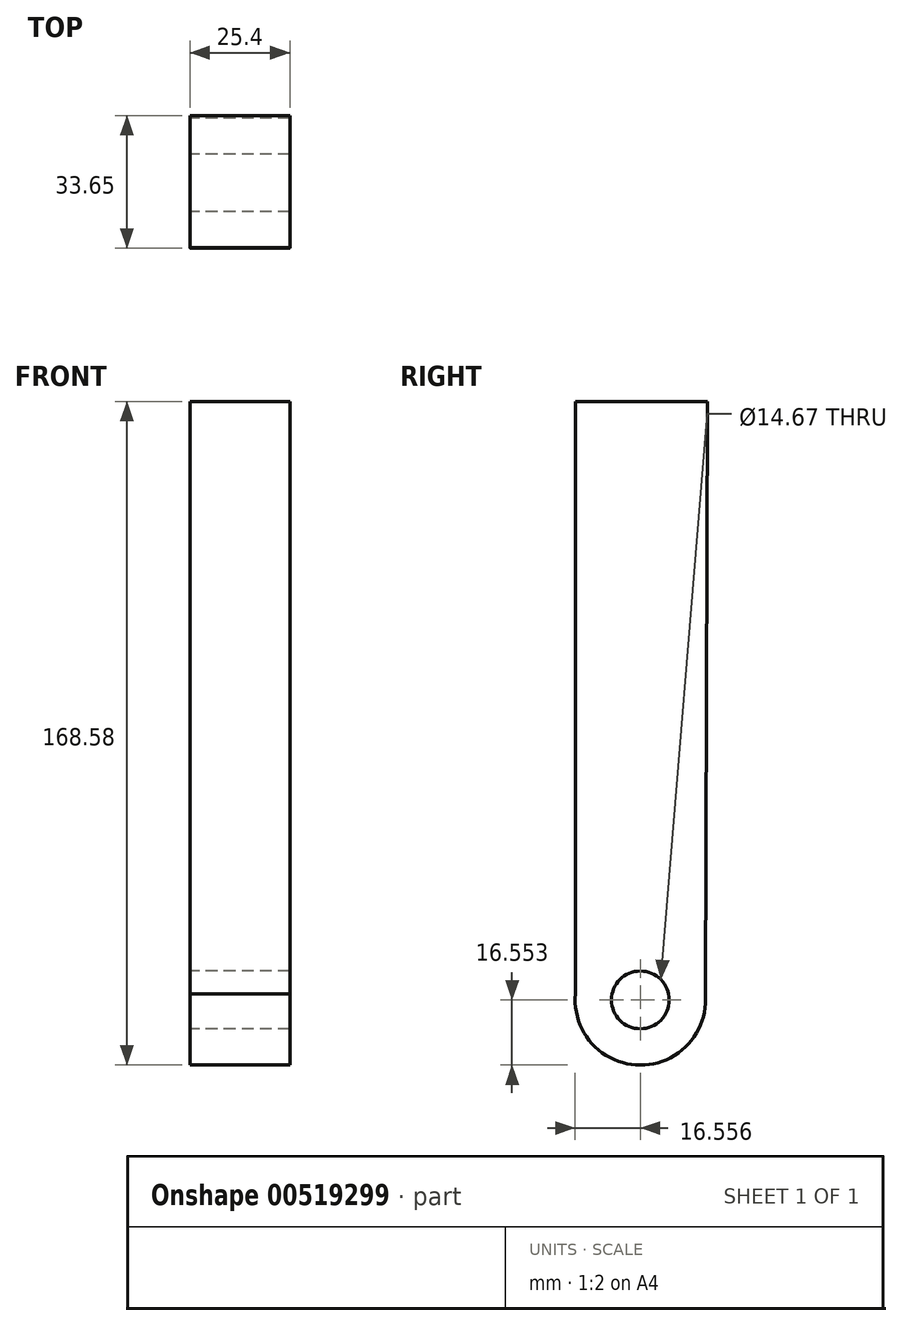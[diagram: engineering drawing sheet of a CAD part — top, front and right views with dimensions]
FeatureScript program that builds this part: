
annotation { "Feature Type Name" : "Feature", "Feature Type Description" : "" }
export const myFeature = defineFeature(function(context is Context, id is Id, definition is map)
    precondition{}
    {
        {
            var Q0;
            Q0=qCreatedBy(makeId("Right.planeOp"),FACE);
            var sketch = newSketch(context, id + "F0", { "sketchPlane" : qUnion([Q0])});
            skLineSegment(sketch, "E0", {"start": v(0, -76.32) * mm, "end": v(-32.97, -76.32) * mm});
            skLineSegment(sketch, "E1", {"start": v(-32.97, -76.32) * mm, "end": v(-32.97, 75.7) * mm});
            skLineSegment(sketch, "E2", {"start": v(-32.97, 75.7) * mm, "end": v(0.61, 75.7) * mm});
            skLineSegment(sketch, "E3", {"start": v(0.61, 75.7) * mm, "end": v(0, -76.32) * mm});
            skCircle(sketch, "E4", {"center": v(-16.48, -76.32) * mm, "radius": 16.55 * mm});
            skCircle(sketch, "E5", {"center": v(-16.48, -76.32) * mm, "radius": 7.33 * mm});
            skSolve(sketch);
        }
        {
            var Q0;
            {var subQ0=sQuery(id+"F0.wireOp",EDGE,"E2");Q0=makeQuery(id+"F0.imprint","IMPRINT",FACE,{"disambiguationData":[TD([[makeQuery(id+"F0.imprint","IMPRINT",EDGE,{"derivedFrom":subQ0}),-1.0]])]});}
            var Q1;
            {var subQ0=sQuery(id+"F0.wireOp",EDGE,"E0");Q1=makeQuery(id+"F0.imprint","IMPRINT",FACE,{"disambiguationData":[TD([[makeQuery(id+"F0.imprint","IMPRINT",EDGE,{"derivedFrom":subQ0}),-1.0]])]});}
            var Q2;
            {var subQ0=sQuery(id+"F0.wireOp",EDGE,"E0");Q2=makeQuery(id+"F0.imprint","IMPRINT",FACE,{"disambiguationData":[TD([[makeQuery(id+"F0.imprint","IMPRINT",EDGE,{"derivedFrom":subQ0}),1.0]])]});}
            extrude(context, id + "F1", {"entities" : qUnion([Q0, Q1, Q2]), "depth" : 25.4 * mm, "offsetDistance" : 25.4 * mm});
        }
    });
